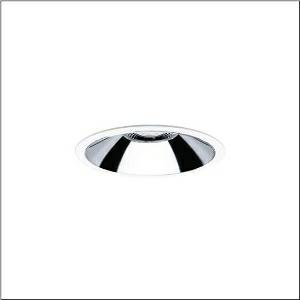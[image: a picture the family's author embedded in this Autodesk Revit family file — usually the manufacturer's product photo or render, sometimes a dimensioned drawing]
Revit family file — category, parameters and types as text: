
# Revit family: lunis_21_xl_51db15df33
name_source: partatom
category: Lighting Fixtures
units: mm (PartAtom-declared; Revit-internal decimal feet)

## family parameters
Cut with Voids When Loaded = No
Host = Face
Light Source = No
Part Type = Normal
Room Calculation Point = No
Round Connector Dimension = Use Diameter
Shared = No

## types (1)
- Lunis 21 XL (1 x LED, 3360 lm, 31 W, 3000K)
    Apparent Load = 31 VA
    CIE Flux Codes = 89 99 100 100 100
    Color Rendering = 80
    Color Temperature = 3000K
    Default Elevation = 1800 mm
    Description = Lunis 21,  XL, downlight, of PC, light emission: direct distribution, LED rated luminous flux: 3.360lm, light colour: 830, control gear: ECG DALI, with terminal, 5-pole, mains connection: 220..240V, AC, housing, round, of diecast aluminium, traffic white (RAL 9016), diameter: 213mm, protection rating (complete): IP20, insulation class (complete): insulation class II (safety insulation), certification: CE, impact resistance: IK02, packaging unit: 1 piece
    Height = 0 mm  [stored 0 ft]
    Lamp = 1 x LED
    Lamp Light Flux = 3360 lm
    Lamp Power = 31 W
    Lamp count = 1
    Length = 213 mm
    Luminous efficacy = 108 lm/W
    Manufacturer = Siteco
    ModVariant = No
    Model = 51DB15DF33
    Mounting Place = Ceiling
    Mounting Type = Recessed
    Number of Poles = 1
    OnlyDefault = Yes
    Power Factor = 1
    Product Name = Lunis 21 XL
    Product group = downlight | ceiling recessed
    ProductGroupID = 402
    Protection Class = Protection class II
    Protection Degree = IP 20
    RLX_Detail_Level = 1
    RlxData = <blob elided: 26909 chars, md5=3c29f092>
    Socket = socket
    Standby Power = 0 W
    System Light Flux = 3360 lm
    System Power = 31 W
    Type Comments = Product without accessories
    Type Image = l_1006990.jpg
    URL = http://relux.com
    VarID = ---
    Voltage = 0 V
    Weight = 0.00 kg
    Width = 0 mm  [stored 0 ft]

note: [stored X ft] marks values corroborated as IEEE doubles in the binary element streams (Revit-internal decimal feet)

## geometry (parser evidence)
native form markers: Blend x4, Sweep x11
no freeform markers — native parametric forms only
